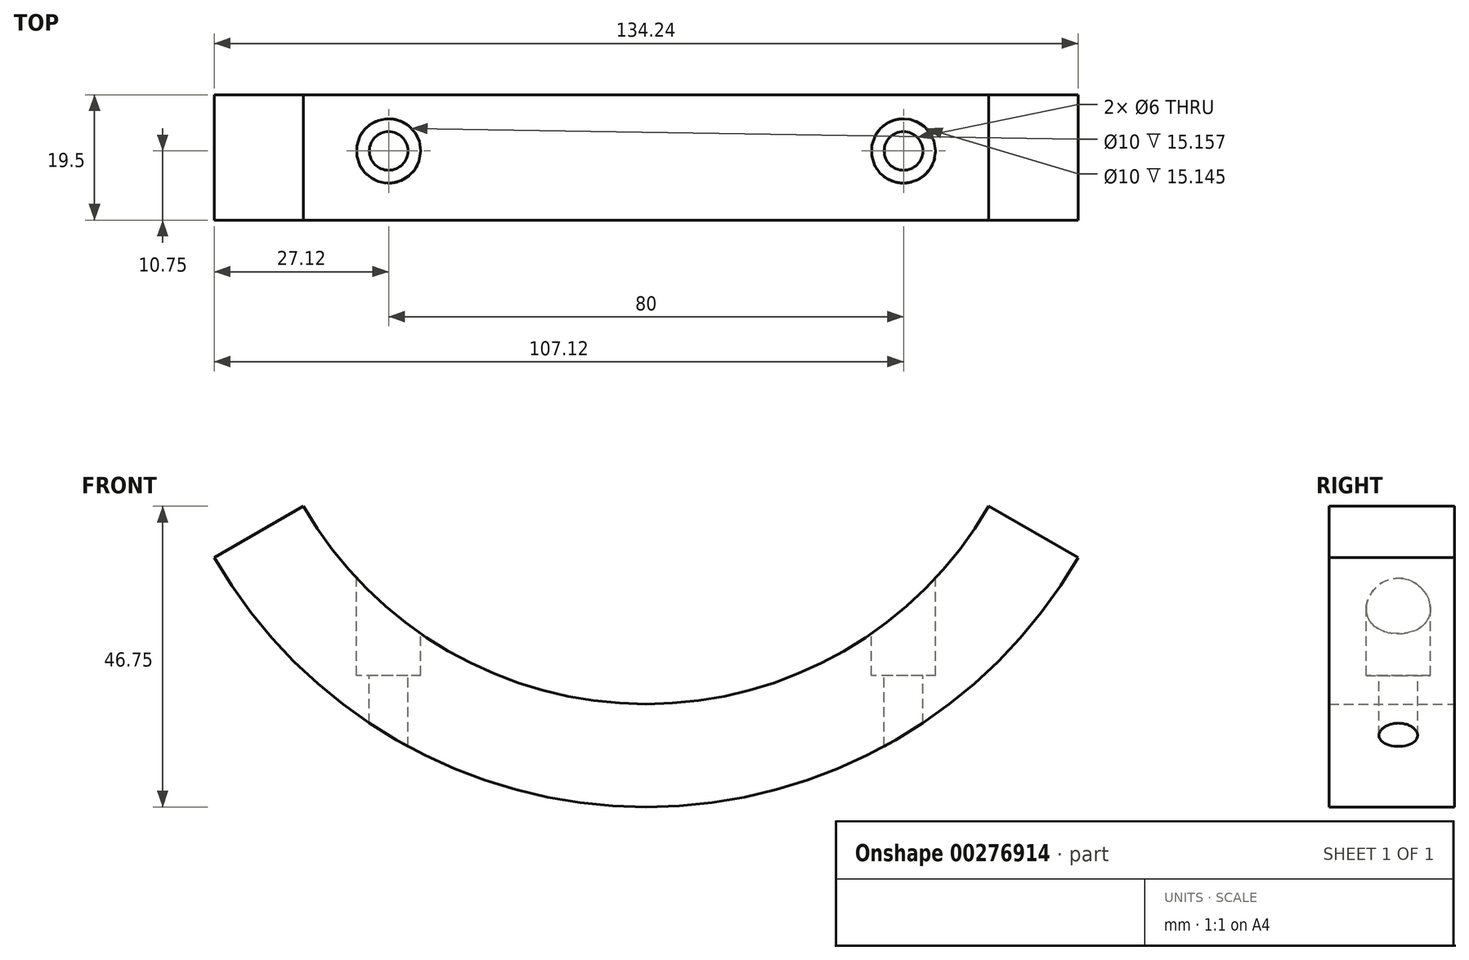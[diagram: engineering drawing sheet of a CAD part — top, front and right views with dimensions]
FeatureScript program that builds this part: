
annotation { "Feature Type Name" : "Feature", "Feature Type Description" : "" }
export const myFeature = defineFeature(function(context is Context, id is Id, definition is map)
    precondition{}
    {
        {
            var Q0;
            Q0=qCreatedBy(makeId("Front.planeOp"),FACE);
            var sketch = newSketch(context, id + "F0", { "sketchPlane" : qUnion([Q0])});
            skLineSegment(sketch, "E0", {"start": v(0, 66.63) * mm, "end": v(0, -19.37) * mm, "construction": true});
            skPoint(sketch, "E0.endSnap0", {"position": v(0, -12) * mm});
            skArc(sketch, "E1", {"start": v(-67.12, 27.88) * mm, "mid": v(0, -10.87) * mm, "end": v(67.12, 27.88) * mm});
            skArc(sketch, "E2", {"start": v(-53.26, 35.88) * mm, "mid": v(0, 5.13) * mm, "end": v(53.26, 35.88) * mm});
            skLineSegment(sketch, "E3", {"start": v(-67.12, 27.88) * mm, "end": v(-53.26, 35.88) * mm});
            skLineSegment(sketch, "E4", {"start": v(53.26, 35.88) * mm, "end": v(67.12, 27.88) * mm});
            skLineSegment(sketch, "E5", {"start": v(0, -10.87) * mm, "end": v(0, 5.13) * mm, "construction": true});
            skSolve(sketch);
        }
        {
            var Q0;
            Q0=qSketchRegion(id+"F0",true);
            extrude(context, id + "F1", {"entities" : qUnion([Q0]), "depth" : 19.5 * mm});
        }
        {
            var Q0;
            Q0=qCreatedBy(makeId("Top.planeOp"),FACE);
            cPlane(context, id + "F2", {"entities" : qUnion([Q0]), "cplaneType" : CPlaneType.OFFSET, "offset" : 50 * mm, "width" : 150 * mm, "height" : 150 * mm});
        }
        {
            var Q0;
            Q0=qCreatedBy(id+"F2.planeOp",FACE);
            var sketch = newSketch(context, id + "F3", { "sketchPlane" : qUnion([Q0])});
            skCircle(sketch, "E6.0", {"center": v(-40, -8.75) * mm, "radius": 3 * mm});
            skCircle(sketch, "E6.1", {"center": v(40, -8.75) * mm, "radius": 3 * mm});
            skCircle(sketch, "E7", {"center": v(-40, -8.75) * mm, "radius": 5 * mm});
            skCircle(sketch, "E8", {"center": v(40, -8.75) * mm, "radius": 5 * mm});
            skSolve(sketch);
        }
        {
            var Q0;
            Q0=makeQuery(id+"F3.imprint","IMPRINT",FACE,{"disambiguationData":[TD([[makeQuery(id+"F3.imprint","IMPRINT",EDGE,{"derivedFrom":sQuery(id+"F3.wireOp",EDGE,"E6.0")}),1.0]])]});
            var Q1;
            Q1=makeQuery(id+"F3.imprint","IMPRINT",FACE,{"disambiguationData":[TD([[makeQuery(id+"F3.imprint","IMPRINT",EDGE,{"derivedFrom":sQuery(id+"F3.wireOp",EDGE,"E6.1")}),1.0]])]});
            extrude(context, id + "F4", {"entities" : qUnion([Q0, Q1]), "operationType" : NewBodyOperationType.REMOVE, "endBound" : BoundingType.THROUGH_ALL, "oppositeDirection" : true, "depth" : 8 * mm});
        }
        {
            var Q0;
            Q0=makeQuery(id+"F3.imprint","IMPRINT",FACE,{"disambiguationData":[TD([[makeQuery(id+"F3.imprint","IMPRINT",EDGE,{"derivedFrom":sQuery(id+"F3.wireOp",EDGE,"E6.1")}),-1.0]])]});
            var Q1;
            Q1=makeQuery(id+"F3.imprint","IMPRINT",FACE,{"disambiguationData":[TD([[makeQuery(id+"F3.imprint","IMPRINT",EDGE,{"derivedFrom":sQuery(id+"F3.wireOp",EDGE,"E6.0")}),-1.0]])]});
            extrude(context, id + "F5", {"entities" : qUnion([Q0, Q1]), "operationType" : NewBodyOperationType.REMOVE, "oppositeDirection" : true, "depth" : 40.43 * mm});
        }
        {
            var Q0;
            Q0=qCreatedBy(makeId("Right.planeOp"),FACE);
            cPlane(context, id + "F6", {"entities" : qUnion([Q0]), "cplaneType" : CPlaneType.OFFSET, "offset" : 32 * mm, "width" : 150 * mm, "height" : 150 * mm});
        }
    });
